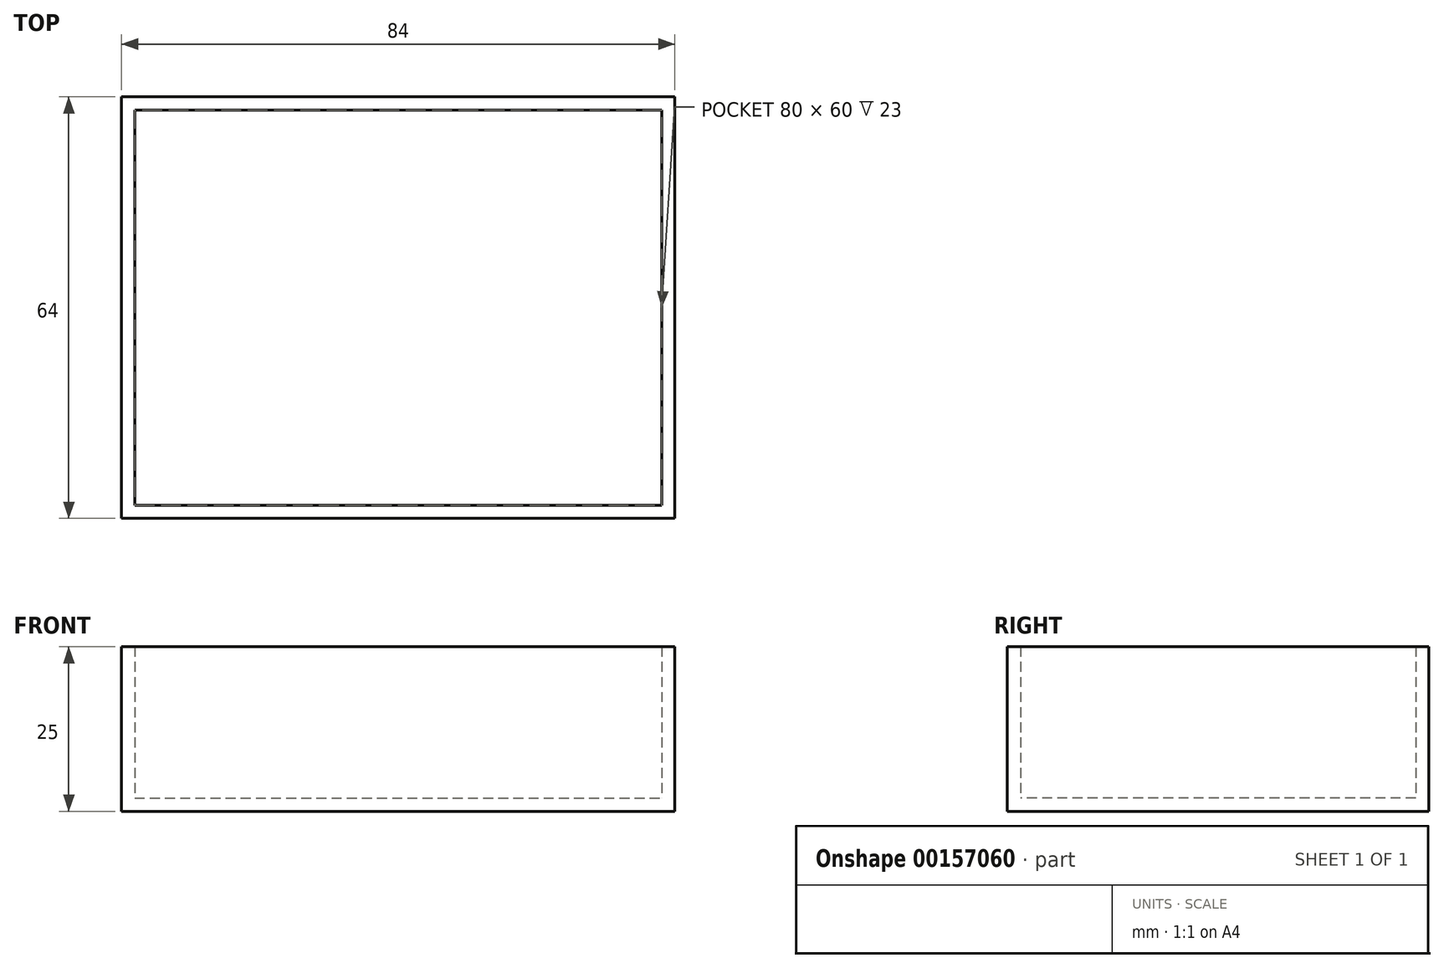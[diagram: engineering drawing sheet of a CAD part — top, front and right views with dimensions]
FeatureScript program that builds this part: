
annotation { "Feature Type Name" : "Feature", "Feature Type Description" : "" }
export const myFeature = defineFeature(function(context is Context, id is Id, definition is map)
    precondition{}
    {
        {
            var Q0;
            Q0=qCreatedBy(makeId("Top.planeOp"),FACE);
            var sketch = newSketch(context, id + "F0", { "sketchPlane" : qUnion([Q0])});
            skLineSegment(sketch, "E0.bottom", {"start": v(-42.39, 27.96) * mm, "end": v(37.61, 27.96) * mm});
            skLineSegment(sketch, "E0.top", {"start": v(-42.39, -32.04) * mm, "end": v(37.61, -32.04) * mm});
            skLineSegment(sketch, "E0.left", {"start": v(-42.39, 27.96) * mm, "end": v(-42.39, -32.04) * mm});
            skLineSegment(sketch, "E0.right", {"start": v(37.61, 27.96) * mm, "end": v(37.61, -32.04) * mm});
            skLineSegment(sketch, "E1.0", {"start": v(-44.39, 29.96) * mm, "end": v(39.61, 29.96) * mm});
            skLineSegment(sketch, "E1.1", {"start": v(-44.39, 29.96) * mm, "end": v(-44.39, -34.04) * mm});
            skLineSegment(sketch, "E1.2", {"start": v(-44.39, -34.04) * mm, "end": v(39.61, -34.04) * mm});
            skLineSegment(sketch, "E1.3", {"start": v(39.61, 29.96) * mm, "end": v(39.61, -34.04) * mm});
            skSolve(sketch);
        }
        {
            var Q0;
            Q0 = qSketchRegion(id + "F0", true);
            extrude(context, id + "F1", {"entities" : qUnion([Q0]), "depth" : 25 * mm});
        }
        {
            var Q0;
            Q0=makeQuery(id+"F0.imprint","IMPRINT",FACE,{"disambiguationData":[TD([[makeQuery(id+"F0.imprint","IMPRINT",EDGE,{"derivedFrom":sQuery(id+"F0.wireOp",EDGE,"E0.bottom")}),-1.0]])]});
            extrude(context, id + "F2", {"entities" : qUnion([Q0]), "operationType" : NewBodyOperationType.ADD, "depth" : 2 * mm});
        }
    });
